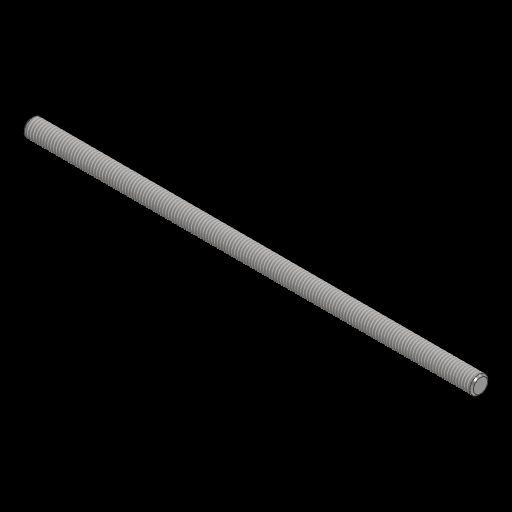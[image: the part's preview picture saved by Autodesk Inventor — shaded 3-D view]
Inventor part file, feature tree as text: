
AUTODESK INVENTOR PART (.ipt)
format: ipt  version: 2024 (Build 280153000, 153)  size: 119,296 bytes
history: native  units: mm
features: revolve x1, chamfer x1, thread x1, sketch x1
ambient origin geometry x8: Origin, YZ Plane, XZ Plane, XY Plane, X Axis, Y Axis, Z Axis, Center Point
bodies: Volumenkörper1 (feature_tree)
feature tree (4):
  revolve  "Umdrehung1"
  chamfer  "Fasen1"  Distance=125.0mm
  thread  "Gewinde1"  [1 undecoded]
  sketch  "Skizze1"  dims[d0=5.0mm d1=125.0mm d2=90.0deg d3=0.5mm d4=2.0mm d5=45.0deg d6=124.0mm d7=0.0mm]
note: 1 required parameter value undecoded (feature->parameter linkage not recoverable at this tier; creation-order binding heuristic only, values carry confidence <= 0.55)
